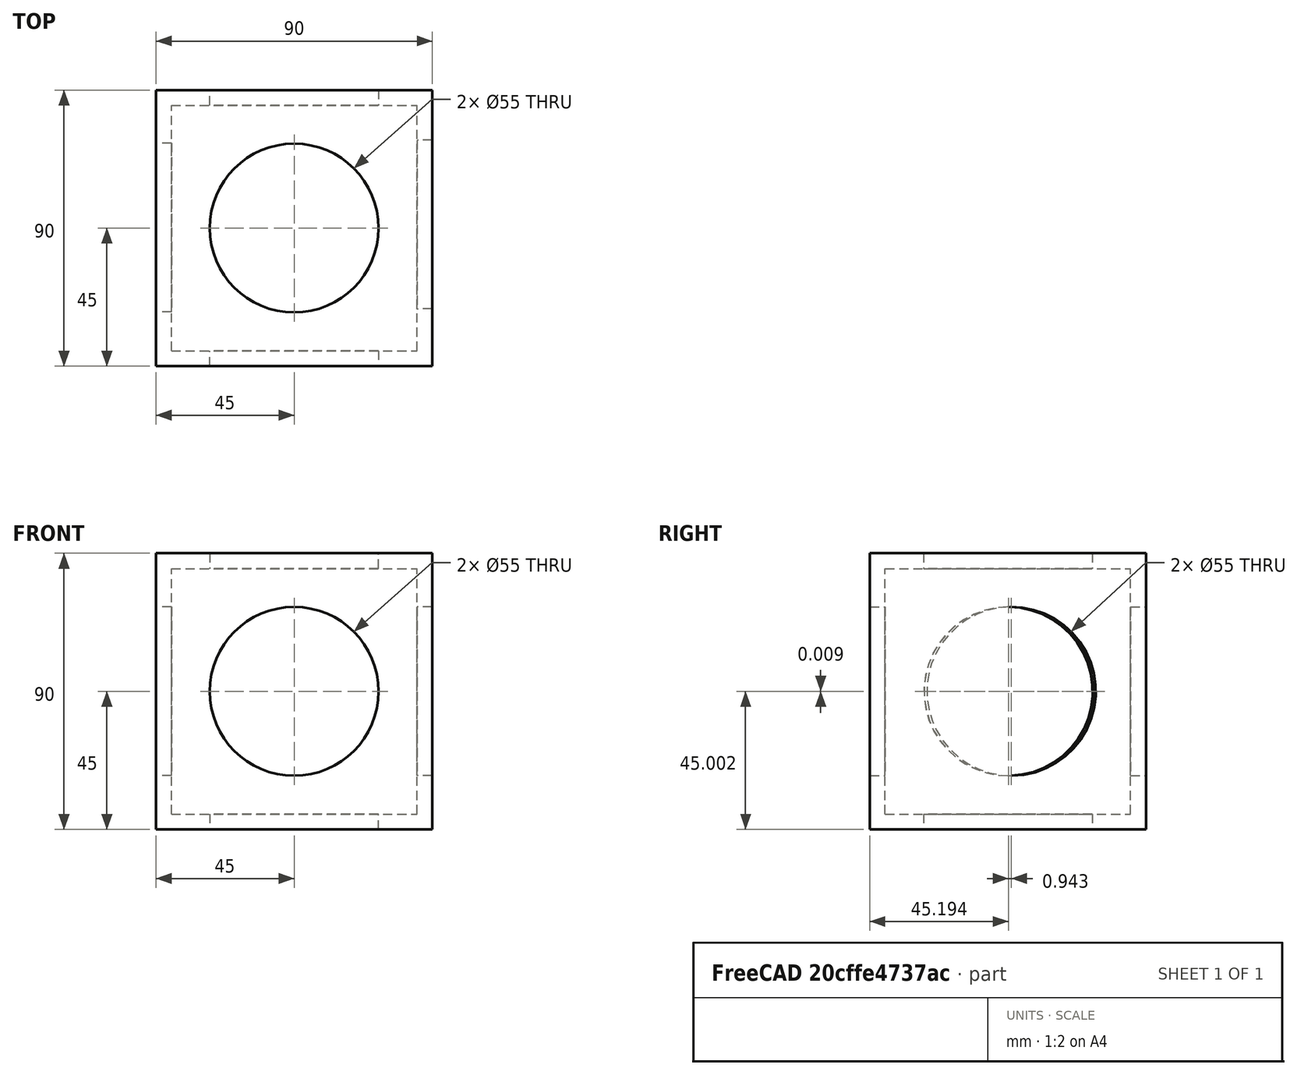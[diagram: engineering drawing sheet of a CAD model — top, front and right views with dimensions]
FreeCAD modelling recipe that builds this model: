
FCSTD DOCUMENT  (FreeCAD 0.20R29603 (Git))
Label: 08.03.2023
License: All rights reserved
LicenseURL: http://en.wikipedia.org/wiki/All_rights_reserved
objects: Part::Cut×4, Part::Cylinder×3, Part::Box×2
note: 9 computed .brp shape members not serialized (recipe doc carries the construction recipe); baked Part::Feature solids carry a one-line shape summary decoded from their .brp

FEATURE [Part::Box] Box  label="Cube"
  AttacherType = Attacher::AttachEngine3D
  Height = 90
  Length = 90
  Placement = pos=(-45,-45,-45) rot=(0,0,1;0rad)
  Width = 90
FEATURE [Part::Box] Box001  label="Cube001"
  AttacherType = Attacher::AttachEngine3D
  Height = 80
  Length = 80
  Placement = pos=(-40,-40,-40) rot=(0,0,1;0rad)
  Width = 80
FEATURE [Part::Cylinder] Cylinder
  Angle = 360
  AttacherType = Attacher::AttachEngine3D
  FirstAngle = 0
  Height = 120
  Placement = pos=(0,0,-60) rot=(0,0,1;0rad)
  Radius = 27.5
  SecondAngle = 0
FEATURE [Part::Cylinder] Cylinder001
  Angle = 360
  AttacherType = Attacher::AttachEngine3D
  FirstAngle = 0
  Height = 120
  Placement = pos=(-60,0,0) rot=(0,0.999938,0.01111;1.5708rad)
  Radius = 27.5
  SecondAngle = 0
FEATURE [Part::Cylinder] Cylinder002
  Angle = 360
  AttacherType = Attacher::AttachEngine3D
  FirstAngle = 0
  Height = 120
  Placement = pos=(0,60,0) rot=(1,0,0;1.5708rad)
  Radius = 27.5
  SecondAngle = 0
FEATURE [Part::Cut] Cut
  Base = -> Box
  Tool = -> Box001
FEATURE [Part::Cut] Cut001
  Base = -> Cut
  Tool = -> Cylinder
FEATURE [Part::Cut] Cut002
  Base = -> Cut001
  Tool = -> Cylinder001
FEATURE [Part::Cut] Cut003
  Base = -> Cut002
  Tool = -> Cylinder002
